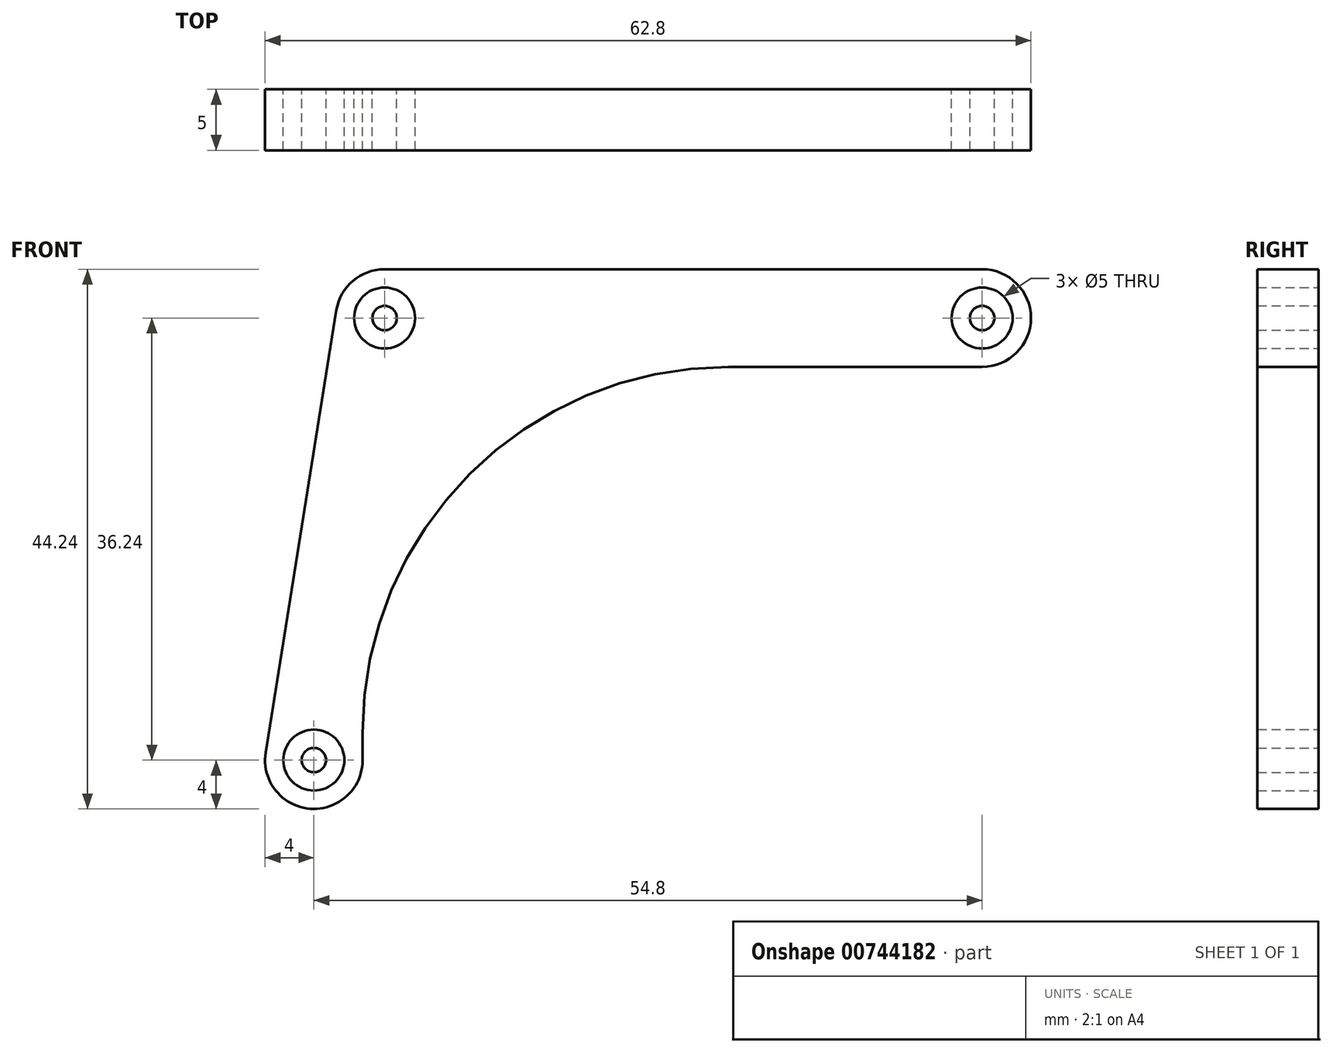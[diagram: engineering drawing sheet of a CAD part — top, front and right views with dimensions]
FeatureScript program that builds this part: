
annotation { "Feature Type Name" : "Feature", "Feature Type Description" : "" }
export const myFeature = defineFeature(function(context is Context, id is Id, definition is map)
    precondition{}
    {
        {
            var Q0;
            Q0=qCreatedBy(makeId("Front.planeOp"),FACE);
            var sketch = newSketch(context, id + "F0", { "sketchPlane" : qUnion([Q0])});
            skArc(sketch, "E0", {"start": v(0, 4) * mm, "mid": v(-2.6, 3.04) * mm, "end": v(-3.95, 0.63) * mm});
            skArc(sketch, "E1", {"start": v(49, -4) * mm, "mid": v(53, 0) * mm, "end": v(49, 4) * mm});
            skCircle(sketch, "E2", {"center": v(-5.8, -36.24) * mm, "radius": 4 * mm});
            skCircle(sketch, "E3", {"center": v(0, 0) * mm, "radius": 2.5 * mm});
            skCircle(sketch, "E4", {"center": v(49, 0) * mm, "radius": 2.5 * mm});
            skCircle(sketch, "E5", {"center": v(-5.8, -36.24) * mm, "radius": 2.5 * mm});
            skLineSegment(sketch, "E6", {"start": v(0, 4) * mm, "end": v(49, 4) * mm});
            skLineSegment(sketch, "E7", {"start": v(49, -4) * mm, "end": v(28.2, -4) * mm});
            skLineSegment(sketch, "E8", {"start": v(-1.8, -34) * mm, "end": v(-1.8, -36.24) * mm});
            skPoint(sketch, "E9.newPointA", {"position": v(0, -4) * mm});
            skPoint(sketch, "E9.newPointB", {"position": v(-1.8, 0) * mm});
            skArc(sketch, "E10", {"start": v(28.2, -4) * mm, "mid": v(6.99, -12.79) * mm, "end": v(-1.8, -34) * mm});
            skPoint(sketch, "E11.orphan", {"position": v(-1.8, -31.76) * mm});
            skLineSegment(sketch, "E12", {"start": v(-3.95, 0.63) * mm, "end": v(-9.75, -35.6) * mm});
            skCircle(sketch, "E13", {"center": v(0, 0) * mm, "radius": 1 * mm});
            skCircle(sketch, "E14", {"center": v(49, 0) * mm, "radius": 1 * mm});
            skCircle(sketch, "E15", {"center": v(-5.8, -36.24) * mm, "radius": 1 * mm});
            skSolve(sketch);
        }
        {
            var Q0;
            Q0=qSketchRegion(id+"F0",true);
            var Q1;
            Q1=makeQuery(id+"F0.imprint","IMPRINT",FACE,{"disambiguationData":[TD([[makeQuery(id+"F0.imprint","IMPRINT",EDGE,{"derivedFrom":sQuery(id+"F0.wireOp",EDGE,"E15")}),1.0]])]});
            var Q2;
            Q2=makeQuery(id+"F0.imprint","IMPRINT",FACE,{"disambiguationData":[TD([[makeQuery(id+"F0.imprint","IMPRINT",EDGE,{"derivedFrom":sQuery(id+"F0.wireOp",EDGE,"E13")}),1.0]])]});
            var Q3;
            Q3=makeQuery(id+"F0.imprint","IMPRINT",FACE,{"disambiguationData":[TD([[makeQuery(id+"F0.imprint","IMPRINT",EDGE,{"derivedFrom":sQuery(id+"F0.wireOp",EDGE,"E14")}),1.0]])]});
            extrude(context, id + "F1", {"entities" : qUnion([Q0, Q1, Q2, Q3]), "depth" : 5 * mm, "offsetDistance" : 25 * mm});
        }
    });
